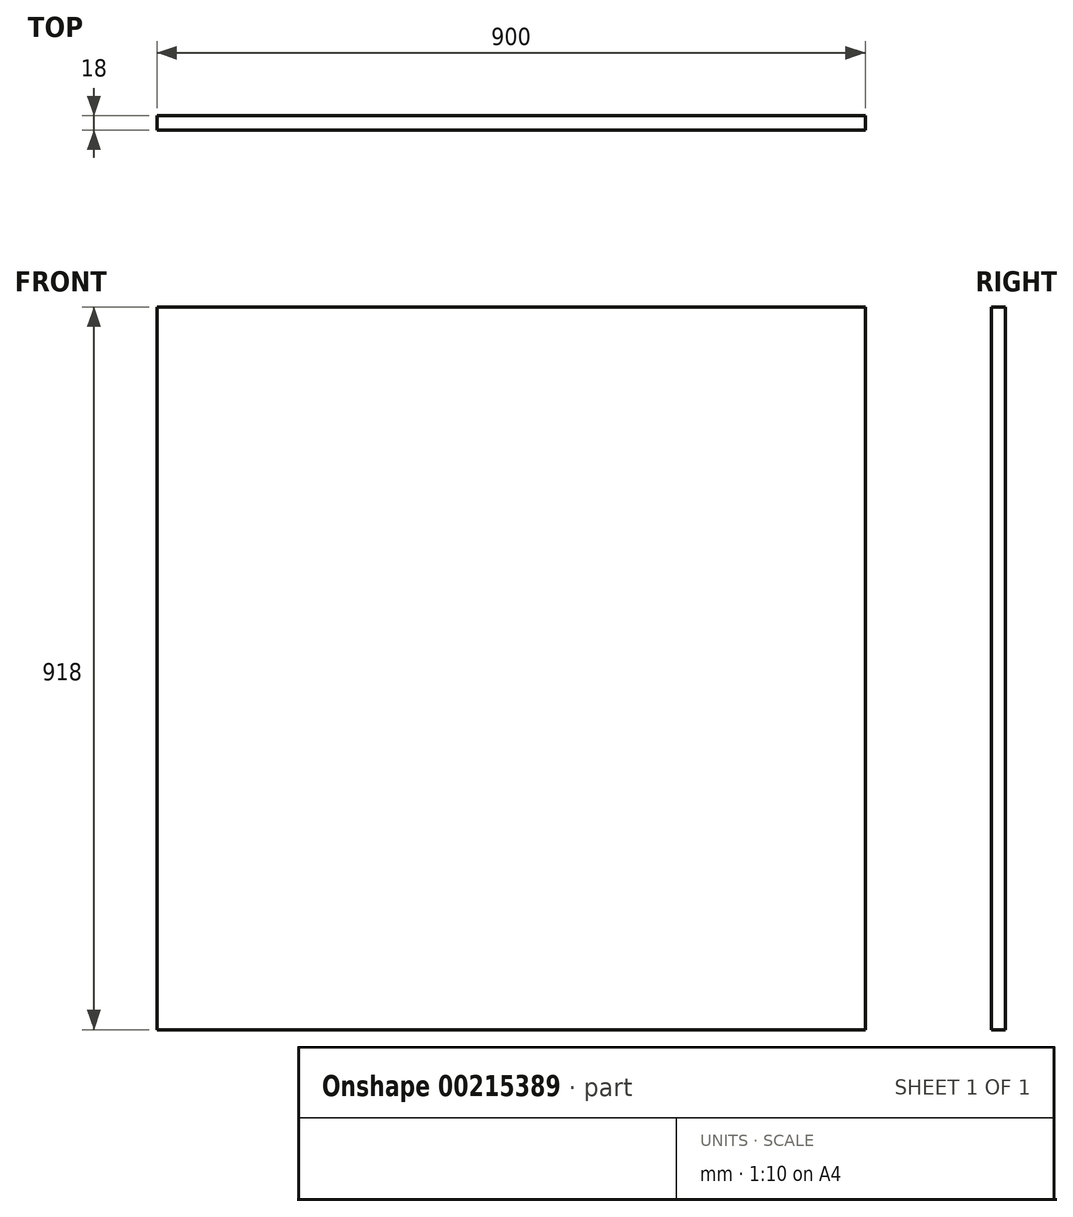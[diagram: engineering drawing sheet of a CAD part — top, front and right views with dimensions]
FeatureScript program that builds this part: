
annotation { "Feature Type Name" : "Feature", "Feature Type Description" : "" }
export const myFeature = defineFeature(function(context is Context, id is Id, definition is map)
    precondition{}
    {
        {
            var Q0;
            Q0=qCreatedBy(makeId("Front.planeOp"),FACE);
            var sketch = newSketch(context, id + "F0", { "sketchPlane" : qUnion([Q0])});
            skLineSegment(sketch, "E0.bottom", {"start": v(-450, -459) * mm, "end": v(450, -459) * mm});
            skLineSegment(sketch, "E0.top", {"start": v(-450, 459) * mm, "end": v(450, 459) * mm});
            skLineSegment(sketch, "E0.left", {"start": v(-450, -459) * mm, "end": v(-450, 459) * mm});
            skLineSegment(sketch, "E0.right", {"start": v(450, -459) * mm, "end": v(450, 459) * mm});
            skPoint(sketch, "E0.middle", {"position": v(0, 0) * mm});
            skSolve(sketch);
        }
        {
            var Q0;
            Q0=makeQuery(id+"F0.imprint","IMPRINT",FACE,{"disambiguationData":[TD([[makeQuery(id+"F0.imprint","IMPRINT",EDGE,{"derivedFrom":sQuery(id+"F0.wireOp",EDGE,"E0.bottom")}),1.0]])]});
            extrude(context, id + "F1", {"entities" : qUnion([Q0]), "depth" : 18 * mm});
        }
    });
